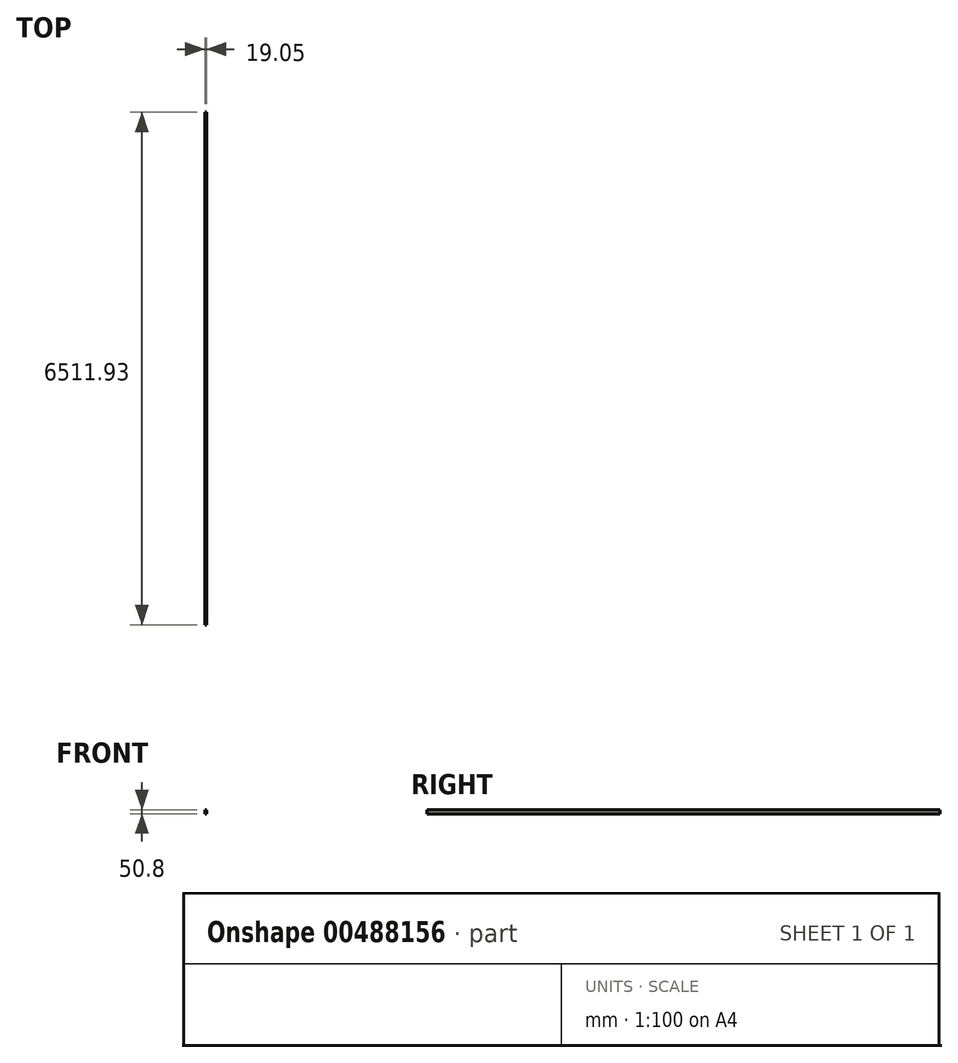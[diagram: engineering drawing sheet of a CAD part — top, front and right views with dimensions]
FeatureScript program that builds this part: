
annotation { "Feature Type Name" : "Feature", "Feature Type Description" : "" }
export const myFeature = defineFeature(function(context is Context, id is Id, definition is map)
    precondition{}
    {
        {
            var Q0;
            Q0=qCreatedBy(makeId("Front.planeOp"),FACE);
            var sketch = newSketch(context, id + "F0", { "sketchPlane" : qUnion([Q0])});
            skLineSegment(sketch, "E0", {"start": v(0, 0) * mm, "end": v(19.05, 0) * mm});
            skLineSegment(sketch, "E1", {"start": v(0, 0) * mm, "end": v(0, -50.8) * mm});
            skLineSegment(sketch, "E2", {"start": v(0, -50.8) * mm, "end": v(19.05, -50.8) * mm});
            skLineSegment(sketch, "E3", {"start": v(19.05, -50.8) * mm, "end": v(19.05, 0) * mm});
            skSolve(sketch);
        }
        {
            var Q0;
            Q0=makeQuery(id+"F0.imprint","IMPRINT",FACE,{"disambiguationData":[TD([[makeQuery(id+"F0.imprint","IMPRINT",EDGE,{"derivedFrom":sQuery(id+"F0.wireOp",EDGE,"E0")}),-1.0]])]});
            extrude(context, id + "F1", {"entities" : qUnion([Q0]), "depth" : 6508.75 * mm + 3.17 * mm, "offsetDistance" : 25.4 * mm});
        }
    });
